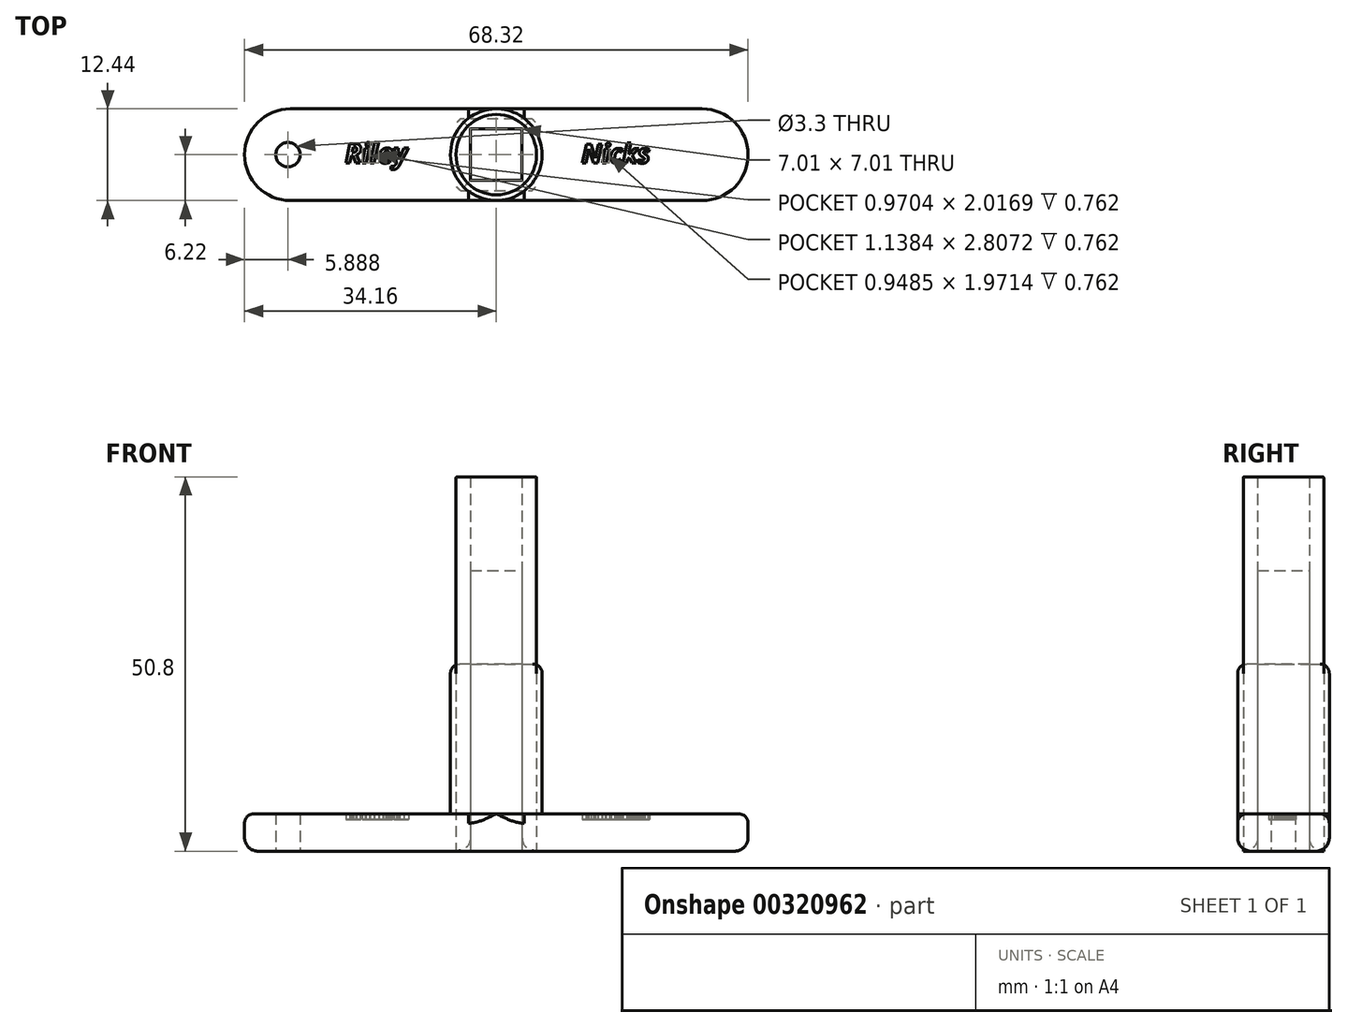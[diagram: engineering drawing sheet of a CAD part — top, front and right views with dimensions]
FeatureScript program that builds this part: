
annotation { "Feature Type Name" : "Feature", "Feature Type Description" : "" }
export const myFeature = defineFeature(function(context is Context, id is Id, definition is map)
    precondition{}
    {
        {
            var Q0;
            Q0=qCreatedBy(makeId("Top.planeOp"),FACE);
            var sketch = newSketch(context, id + "F0", { "sketchPlane" : qUnion([Q0])});
            skLineSegment(sketch, "E0", {"start": v(-27.94, 6.22) * mm, "end": v(0, 6.22) * mm});
            skLineSegment(sketch, "E1", {"start": v(0, 6.22) * mm, "end": v(27.94, 6.22) * mm});
            skLineSegment(sketch, "E2", {"start": v(0, -6.22) * mm, "end": v(-27.94, -6.22) * mm});
            skLineSegment(sketch, "E3", {"start": v(0, -6.22) * mm, "end": v(27.94, -6.22) * mm});
            skArc(sketch, "E4", {"start": v(-27.94, 6.22) * mm, "mid": v(-34.16, 0) * mm, "end": v(-27.94, -6.22) * mm});
            skArc(sketch, "E5", {"start": v(27.94, -6.22) * mm, "mid": v(34.16, 0) * mm, "end": v(27.94, 6.22) * mm});
            skLineSegment(sketch, "E6", {"start": v(-39.69, 0) * mm, "end": v(47.84, 0) * mm, "construction": true});
            skSolve(sketch);
        }
        {
            var Q0;
            Q0=makeQuery(id+"F0.imprint","IMPRINT",FACE,{"disambiguationData":[TD([[makeQuery(id+"F0.imprint","IMPRINT",EDGE,{"derivedFrom":sQuery(id+"F0.wireOp",EDGE,"E0")}),-1.0]])]});
            extrude(context, id + "F1", {"entities" : qUnion([Q0]), "depth" : 5.08 * mm});
        }
        {
            var Q0;
            Q0=qCreatedBy(makeId("Top.planeOp"),FACE);
            var sketch = newSketch(context, id + "F2", { "sketchPlane" : qUnion([Q0])});
            skCircle(sketch, "E7", {"center": v(0, 0) * mm, "radius": 6.22 * mm});
            skSolve(sketch);
        }
        {
            var Q0;
            Q0=makeQuery(id+"F2.imprint","IMPRINT",FACE,{"disambiguationData":[TD([[makeQuery(id+"F2.imprint","IMPRINT",EDGE,{"derivedFrom":sQuery(id+"F2.wireOp",EDGE,"E7")}),1.0]])]});
            extrude(context, id + "F3", {"entities" : qUnion([Q0]), "operationType" : NewBodyOperationType.ADD, "depth" : 25.4 * mm});
        }
        {
            var Q0;
            Q0=qCreatedBy(makeId("Top.planeOp"),FACE);
            var sketch = newSketch(context, id + "F4", { "sketchPlane" : qUnion([Q0])});
            skCircle(sketch, "E8", {"center": v(0, 0) * mm, "radius": 5.46 * mm});
            skSolve(sketch);
        }
        {
            var Q0;
            Q0=makeQuery(id+"F4.imprint","IMPRINT",FACE,{"disambiguationData":[TD([[makeQuery(id+"F4.imprint","IMPRINT",EDGE,{"derivedFrom":sQuery(id+"F4.wireOp",EDGE,"E8")}),1.0]])]});
            var Q1;
            Q1=sQuery(id+"F4.wireOp",EDGE,"E8");
            extrude(context, id + "F5", {"entities" : qUnion([Q0]), "surfaceEntities" : qUnion([Q1]), "depth" : 50.8 * mm});
        }
        {
            var Q0;
            Q0=qCreatedBy(makeId("Top.planeOp"),FACE);
            var sketch = newSketch(context, id + "F6", { "sketchPlane" : qUnion([Q0])});
            skLineSegment(sketch, "E9", {"start": v(0, -24.9) * mm, "end": v(0, 17.9) * mm, "construction": true});
            skLineSegment(sketch, "E10", {"start": v(-43.84, 0) * mm, "end": v(50.9, 0) * mm, "construction": true});
            skLineSegment(sketch, "E11", {"start": v(-3.5, -3.5) * mm, "end": v(-3.5, 3.5) * mm});
            skLineSegment(sketch, "E12", {"start": v(3.5, -3.5) * mm, "end": v(3.5, 3.5) * mm});
            skPoint(sketch, "E12.startSnap0", {"position": v(0, -3.5) * mm});
            skLineSegment(sketch, "E13", {"start": v(-3.5, -3.5) * mm, "end": v(3.5, -3.5) * mm});
            skLineSegment(sketch, "E14", {"start": v(-3.5, 3.5) * mm, "end": v(3.5, 3.5) * mm});
            skSolve(sketch);
        }
        {
            var Q0;
            Q0 = qSketchRegion(id + "F6", true);
            extrude(context, id + "F7", {"entities" : qUnion([Q0]), "operationType" : NewBodyOperationType.REMOVE, "endBound" : BoundingType.THROUGH_ALL, "depth" : 25.4 * mm});
        }
        {
            var Q0;
            Q0 = qSketchRegion(id + "F6", true);
            extrude(context, id + "F8", {"entities" : qUnion([Q0]), "depth" : 38.1 * mm});
        }
        {
            var Q0;
            Q0=makeQuery(id+"F1.opExtrude","CAP_FACE",FACE,{"disambiguationData":[OSD([sQuery(id+"F0.wireOp",EDGE,"E0"),sQuery(id+"F0.wireOp",EDGE,"E1"),sQuery(id+"F0.wireOp",EDGE,"E2"),sQuery(id+"F0.wireOp",EDGE,"E3"),sQuery(id+"F0.wireOp",EDGE,"E4"),sQuery(id+"F0.wireOp",EDGE,"E5")])],"isStart":true});
            fillet(context, id + "F9", {"entities" : qUnion([Q0]), "radius" : 1.84 * mm, "tangentPropagation" : true, "allowEdgeOverflow" : false});
        }
        {
            var Q0;
            {var subQ0=sQuery(id+"F0.wireOp",EDGE,"E1");var subQ1=sQuery(id+"F0.wireOp",EDGE,"E0");var subQ2=sQuery(id+"F0.wireOp",EDGE,"E5");Q0=makeQuery(id+"F3.boolean.opBoolean","SPLIT",EDGE,{"disambiguationData":[TD([makeQuery(id+"F1.opExtrude","SWEPT_FACE",FACE,{"disambiguationData":[OSD([subQ2])]})])],"derivedFrom":makeQuery(id+"F1.opExtrude","CAP_EDGE",EDGE,{"disambiguationData":[OSD([subQ1,subQ0])],"isStart":false})});}
            var Q1;
            Q1=makeQuery(id+"F1.opExtrude","CAP_EDGE",EDGE,{"disambiguationData":[OSD([sQuery(id+"F0.wireOp",EDGE,"E5")])],"isStart":false});
            var Q2;
            {var subQ0=sQuery(id+"F0.wireOp",EDGE,"E5");var subQ1=sQuery(id+"F0.wireOp",EDGE,"E3");var subQ2=sQuery(id+"F0.wireOp",EDGE,"E2");Q2=makeQuery(id+"F3.boolean.opBoolean","SPLIT",EDGE,{"disambiguationData":[TD([makeQuery(id+"F1.opExtrude","SWEPT_FACE",FACE,{"disambiguationData":[OSD([subQ0])]})])],"derivedFrom":makeQuery(id+"F1.opExtrude","CAP_EDGE",EDGE,{"disambiguationData":[OSD([subQ2,subQ1])],"isStart":false})});}
            var Q3;
            {var subQ0=sQuery(id+"F0.wireOp",EDGE,"E4");var subQ1=sQuery(id+"F0.wireOp",EDGE,"E3");var subQ2=sQuery(id+"F0.wireOp",EDGE,"E2");Q3=makeQuery(id+"F3.boolean.opBoolean","SPLIT",EDGE,{"disambiguationData":[TD([makeQuery(id+"F1.opExtrude","SWEPT_FACE",FACE,{"disambiguationData":[OSD([subQ0])]})])],"derivedFrom":makeQuery(id+"F1.opExtrude","CAP_EDGE",EDGE,{"disambiguationData":[OSD([subQ2,subQ1])],"isStart":false})});}
            var Q4;
            Q4=makeQuery(id+"F1.opExtrude","CAP_EDGE",EDGE,{"disambiguationData":[OSD([sQuery(id+"F0.wireOp",EDGE,"E4")])],"isStart":false});
            var Q5;
            {var subQ0=sQuery(id+"F0.wireOp",EDGE,"E1");var subQ1=sQuery(id+"F0.wireOp",EDGE,"E0");var subQ2=sQuery(id+"F0.wireOp",EDGE,"E4");Q5=makeQuery(id+"F3.boolean.opBoolean","SPLIT",EDGE,{"disambiguationData":[TD([makeQuery(id+"F1.opExtrude","SWEPT_FACE",FACE,{"disambiguationData":[OSD([subQ2])]})])],"derivedFrom":makeQuery(id+"F1.opExtrude","CAP_EDGE",EDGE,{"disambiguationData":[OSD([subQ1,subQ0])],"isStart":false})});}
            fillet(context, id + "F10", {"entities" : qUnion([Q0, Q1, Q2, Q3, Q4, Q5]), "radius" : 1.27 * mm, "allowEdgeOverflow" : false});
        }
        {
            var Q0;
            Q0=qCreatedBy(makeId("Top.planeOp"),FACE);
            var sketch = newSketch(context, id + "F11", { "sketchPlane" : qUnion([Q0])});
            skText(sketch, "E15", { "text": "Riley", "fontName": "OpenSans-BoldItalic.ttf"});
            skText(sketch, "E16", { "text": "Nicks", "fontName": "OpenSans-BoldItalic.ttf"});
            const initialGuessF11  = {"E15": [-0.02052, -0.00114, 1, 0, 0.00266], "E16": [0.01158, -0.00114, 1, 0, 0.0026]};
            skSetInitialGuess(sketch, initialGuessF11);
            skSolve(sketch);
        }
        {
            var Q0;
            Q0 = qSketchRegion(id + "F11", true);
            extrude(context, id + "F12", {"entities" : qUnion([Q0]), "operationType" : NewBodyOperationType.REMOVE, "endBound" : BoundingType.THROUGH_ALL, "depth" : 25.4 * mm});
        }
        {
            var Q0;
            Q0 = qSketchRegion(id + "F11", true);
            extrude(context, id + "F13", {"entities" : qUnion([Q0]), "operationType" : NewBodyOperationType.ADD, "depth" : 4.32 * mm});
        }
        {
            var Q0;
            Q0=qCreatedBy(makeId("Top.planeOp"),FACE);
            var sketch = newSketch(context, id + "F14", { "sketchPlane" : qUnion([Q0])});
            skCircle(sketch, "E17", {"center": v(-28.27, 0) * mm, "radius": 1.65 * mm});
            skSolve(sketch);
        }
        {
            var Q0;
            Q0 = qSketchRegion(id + "F14", true);
            extrude(context, id + "F15", {"entities" : qUnion([Q0]), "operationType" : NewBodyOperationType.REMOVE, "endBound" : BoundingType.THROUGH_ALL, "depth" : 25.4 * mm});
        }
        {
            var Q0;
            Q0=makeQuery(id+"F3.opExtrude","CAP_EDGE",EDGE,{"disambiguationData":[OSD([sQuery(id+"F2.wireOp",EDGE,"E7")])],"isStart":false});
            fillet(context, id + "F16", {"entities" : qUnion([Q0]), "radius" : 1.27 * mm, "tangentPropagation" : true, "allowEdgeOverflow" : false});
        }
        {
            var Q0;
            Q0=makeQuery(id+"F5.opExtrude","CAP_EDGE",EDGE,{"disambiguationData":[OSD([sQuery(id+"F4.wireOp",EDGE,"E8")])],"isStart":false});
            fillet(context, id + "F17", {"entities" : qUnion([Q0]), "radius" : 0.13 * mm, "tangentPropagation" : true, "allowEdgeOverflow" : false});
        }
    });
